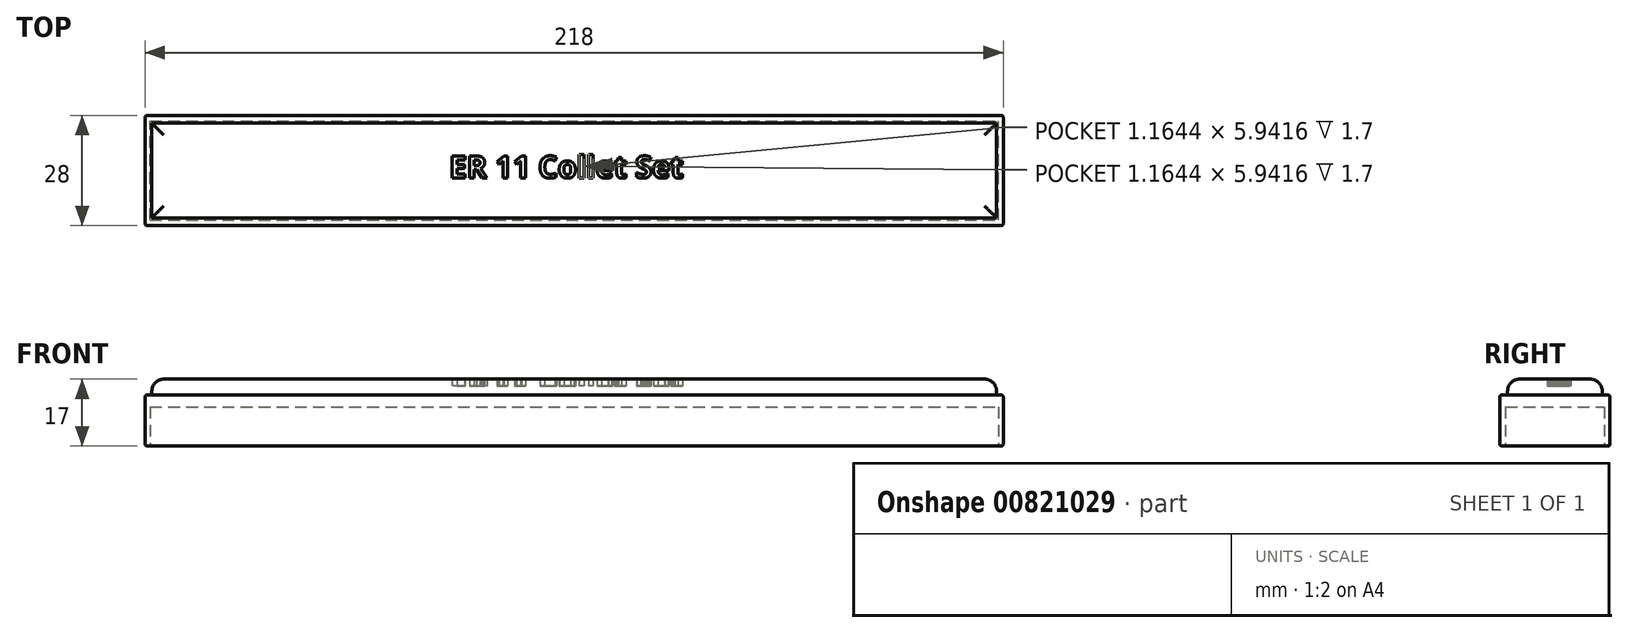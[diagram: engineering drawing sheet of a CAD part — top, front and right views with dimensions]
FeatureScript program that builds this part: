
annotation { "Feature Type Name" : "Feature", "Feature Type Description" : "" }
export const myFeature = defineFeature(function(context is Context, id is Id, definition is map)
    precondition{}
    {
        {
            var Q0;
            Q0=qCreatedBy(makeId("Top.planeOp"),FACE);
            var sketch = newSketch(context, id + "F0", { "sketchPlane" : qUnion([Q0])});
            skLineSegment(sketch, "E0.bottom", {"start": v(-109, 14) * mm, "end": v(109, 14) * mm});
            skLineSegment(sketch, "E0.top", {"start": v(-109, -14) * mm, "end": v(109, -14) * mm});
            skLineSegment(sketch, "E0.left", {"start": v(-109, 14) * mm, "end": v(-109, -14) * mm});
            skLineSegment(sketch, "E0.right", {"start": v(109, 14) * mm, "end": v(109, -14) * mm});
            skPoint(sketch, "E0.middle", {"position": v(0, 0) * mm});
            skLineSegment(sketch, "E1.bottom", {"start": v(-107.75, -12.6) * mm, "end": v(107.75, -12.6) * mm});
            skLineSegment(sketch, "E1.top", {"start": v(-107.75, 12.6) * mm, "end": v(107.75, 12.6) * mm});
            skLineSegment(sketch, "E1.left", {"start": v(-107.75, -12.6) * mm, "end": v(-107.75, 12.6) * mm});
            skLineSegment(sketch, "E1.right", {"start": v(107.75, -12.6) * mm, "end": v(107.75, 12.6) * mm});
            skSolve(sketch);
        }
        {
            var Q0;
            Q0=qSketchRegion(id+"F0",true);
            extrude(context, id + "F1", {"entities" : qUnion([Q0]), "depth" : 10 * mm, "offsetDistance" : 25 * mm});
        }
        {
            var Q0;
            Q0=makeQuery(id+"F1.opExtrude","CAP_FACE",FACE,{"disambiguationData":[OSD([sQuery(id+"F0.wireOp",EDGE,"E0.bottom"),sQuery(id+"F0.wireOp",EDGE,"E0.top"),sQuery(id+"F0.wireOp",EDGE,"E0.left"),sQuery(id+"F0.wireOp",EDGE,"E0.right"),sQuery(id+"F0.wireOp",EDGE,"E1.bottom"),sQuery(id+"F0.wireOp",EDGE,"E1.top"),sQuery(id+"F0.wireOp",EDGE,"E1.left"),sQuery(id+"F0.wireOp",EDGE,"E1.right")])],"isStart":false});
            var sketch = newSketch(context, id + "F2", { "sketchPlane" : qUnion([Q0])});
            skLineSegment(sketch, "E2.bottom", {"start": v(109, -14) * mm, "end": v(-109, -14) * mm});
            skLineSegment(sketch, "E2.top", {"start": v(109, 14) * mm, "end": v(-109, 14) * mm});
            skLineSegment(sketch, "E2.left", {"start": v(109, -14) * mm, "end": v(109, 14) * mm});
            skLineSegment(sketch, "E2.right", {"start": v(-109, -14) * mm, "end": v(-109, 14) * mm});
            skPoint(sketch, "E2.middle", {"position": v(0, 0) * mm});
            skText(sketch, "E3", { "text": "ER 11 Collet Set", "fontName": "OpenSans-Bold.ttf"});
            const initialGuessF2  = {"E3": [-0.03167, 0.03052, 1, 0, 0.00563]};
            skSetInitialGuess(sketch, initialGuessF2);
            skSolve(sketch);
        }
        {
            var Q0;
            Q0=qSketchRegion(id+"F2",true);
            extrude(context, id + "F3", {"entities" : qUnion([Q0]), "operationType" : NewBodyOperationType.ADD, "depth" : 3 * mm, "offsetDistance" : 25 * mm});
        }
        {
            var Q0;
            Q0=makeQuery(id+"F1.opExtrude","CAP_EDGE",EDGE,{"disambiguationData":[OSD([sQuery(id+"F0.wireOp",EDGE,"E0.top")])],"isStart":true});
            var Q1;
            Q1=makeQuery(id+"F1.opExtrude","CAP_EDGE",EDGE,{"disambiguationData":[OSD([sQuery(id+"F0.wireOp",EDGE,"E0.left")])],"isStart":true});
            var Q2;
            Q2=makeQuery(id+"F1.opExtrude","CAP_EDGE",EDGE,{"disambiguationData":[OSD([sQuery(id+"F0.wireOp",EDGE,"E0.right")])],"isStart":true});
            var Q3;
            Q3=makeQuery(id+"F3.boolean.opBoolean","MERGE",EDGE,{"derivedFrom":[makeQuery(id+"F1.opExtrude","SWEPT_EDGE",EDGE,{"disambiguationData":[OSD([sQuery(id+"F0.wireOp",EDGE,"E0.top"),sQuery(id+"F0.wireOp",EDGE,"E0.right")])]}),makeQuery(id+"F3.opExtrude","SWEPT_EDGE",EDGE,{"disambiguationData":[OSD([sQuery(id+"F2.wireOp",EDGE,"E2.bottom"),sQuery(id+"F2.wireOp",EDGE,"E2.left")])]})]});
            var Q4;
            Q4=makeQuery(id+"F3.opExtrude","CAP_EDGE",EDGE,{"disambiguationData":[OSD([sQuery(id+"F2.wireOp",EDGE,"E2.bottom")])],"isStart":false});
            var Q5;
            Q5=makeQuery(id+"F3.opExtrude","CAP_EDGE",EDGE,{"disambiguationData":[OSD([sQuery(id+"F2.wireOp",EDGE,"E2.left")])],"isStart":false});
            var Q6;
            Q6=makeQuery(id+"F3.opExtrude","CAP_EDGE",EDGE,{"disambiguationData":[OSD([sQuery(id+"F2.wireOp",EDGE,"E2.top")])],"isStart":false});
            var Q7;
            Q7=makeQuery(id+"F3.boolean.opBoolean","MERGE",FACE,{"derivedFrom":[makeQuery(id+"F1.opExtrude","SWEPT_FACE",FACE,{"disambiguationData":[OSD([sQuery(id+"F0.wireOp",EDGE,"E0.bottom")])]}),makeQuery(id+"F3.opExtrude","SWEPT_FACE",FACE,{"disambiguationData":[OSD([sQuery(id+"F2.wireOp",EDGE,"E2.top")])]})]});
            var Q8;
            Q8=makeQuery(id+"F1.opExtrude","CAP_EDGE",EDGE,{"disambiguationData":[OSD([sQuery(id+"F0.wireOp",EDGE,"E0.bottom")])],"isStart":true});
            var Q9;
            Q9=makeQuery(id+"F3.opExtrude","CAP_EDGE",EDGE,{"disambiguationData":[OSD([sQuery(id+"F2.wireOp",EDGE,"E2.right")])],"isStart":false});
            var Q10;
            Q10=makeQuery(id+"F3.boolean.opBoolean","MERGE",EDGE,{"derivedFrom":[makeQuery(id+"F1.opExtrude","SWEPT_EDGE",EDGE,{"disambiguationData":[OSD([sQuery(id+"F0.wireOp",EDGE,"E0.top"),sQuery(id+"F0.wireOp",EDGE,"E0.left")])]}),makeQuery(id+"F3.opExtrude","SWEPT_EDGE",EDGE,{"disambiguationData":[OSD([sQuery(id+"F2.wireOp",EDGE,"E2.bottom"),sQuery(id+"F2.wireOp",EDGE,"E2.right")])]})]});
            fillet(context, id + "F4", {"entities" : qUnion([Q0, Q1, Q2, Q3, Q4, Q5, Q6, Q7, Q8, Q9, Q10]), "radius" : .5 * mm, "tangentPropagation" : true, "allowEdgeOverflow" : false});
        }
        {
            var Q0;
            Q0=makeQuery(id+"F3.opExtrude","CAP_FACE",FACE,{"disambiguationData":[OSD([sQuery(id+"F2.wireOp",EDGE,"E2.bottom"),sQuery(id+"F2.wireOp",EDGE,"E2.top"),sQuery(id+"F2.wireOp",EDGE,"E2.left"),sQuery(id+"F2.wireOp",EDGE,"E2.right"),sQuery(id+"F2.wireOp",EDGE,"E3.sketch_text.stroke-0"),sQuery(id+"F2.wireOp",EDGE,"E3.sketch_text.stroke-1"),sQuery(id+"F2.wireOp",EDGE,"E3.sketch_text.stroke-2"),sQuery(id+"F2.wireOp",EDGE,"E3.sketch_text.stroke-3"),sQuery(id+"F2.wireOp",EDGE,"E3.sketch_text.stroke-4"),sQuery(id+"F2.wireOp",EDGE,"E3.sketch_text.stroke-5"),sQuery(id+"F2.wireOp",EDGE,"E3.sketch_text.stroke-6"),sQuery(id+"F2.wireOp",EDGE,"E3.sketch_text.stroke-7"),sQuery(id+"F2.wireOp",EDGE,"E3.sketch_text.stroke-8"),sQuery(id+"F2.wireOp",EDGE,"E3.sketch_text.stroke-9"),sQuery(id+"F2.wireOp",EDGE,"E3.sketch_text.stroke-10"),sQuery(id+"F2.wireOp",EDGE,"E3.sketch_text.stroke-11"),sQuery(id+"F2.wireOp",EDGE,"E3.sketch_text.stroke-19"),sQuery(id+"F2.wireOp",EDGE,"E3.sketch_text.stroke-20"),sQuery(id+"F2.wireOp",EDGE,"E3.sketch_text.stroke-21"),sQuery(id+"F2.wireOp",EDGE,"E3.sketch_text.stroke-22"),sQuery(id+"F2.wireOp",EDGE,"E3.sketch_text.stroke-23"),sQuery(id+"F2.wireOp",EDGE,"E3.sketch_text.stroke-24"),sQuery(id+"F2.wireOp",EDGE,"E3.sketch_text.stroke-25"),sQuery(id+"F2.wireOp",EDGE,"E3.sketch_text.stroke-26"),sQuery(id+"F2.wireOp",EDGE,"E3.sketch_text.stroke-27"),sQuery(id+"F2.wireOp",EDGE,"E3.sketch_text.stroke-28"),sQuery(id+"F2.wireOp",EDGE,"E3.sketch_text.stroke-29"),sQuery(id+"F2.wireOp",EDGE,"E3.sketch_text.stroke-30"),sQuery(id+"F2.wireOp",EDGE,"E3.sketch_text.stroke-31"),sQuery(id+"F2.wireOp",EDGE,"E3.sketch_text.stroke-32"),sQuery(id+"F2.wireOp",EDGE,"E3.sketch_text.stroke-33"),sQuery(id+"F2.wireOp",EDGE,"E3.sketch_text.stroke-34"),sQuery(id+"F2.wireOp",EDGE,"E3.sketch_text.stroke-35"),sQuery(id+"F2.wireOp",EDGE,"E3.sketch_text.stroke-36"),sQuery(id+"F2.wireOp",EDGE,"E3.sketch_text.stroke-37"),sQuery(id+"F2.wireOp",EDGE,"E3.sketch_text.stroke-38"),sQuery(id+"F2.wireOp",EDGE,"E3.sketch_text.stroke-39"),sQuery(id+"F2.wireOp",EDGE,"E3.sketch_text.stroke-40"),sQuery(id+"F2.wireOp",EDGE,"E3.sketch_text.stroke-41"),sQuery(id+"F2.wireOp",EDGE,"E3.sketch_text.stroke-42"),sQuery(id+"F2.wireOp",EDGE,"E3.sketch_text.stroke-43"),sQuery(id+"F2.wireOp",EDGE,"E3.sketch_text.stroke-44"),sQuery(id+"F2.wireOp",EDGE,"E3.sketch_text.stroke-45"),sQuery(id+"F2.wireOp",EDGE,"E3.sketch_text.stroke-46"),sQuery(id+"F2.wireOp",EDGE,"E3.sketch_text.stroke-47"),sQuery(id+"F2.wireOp",EDGE,"E3.sketch_text.stroke-48"),sQuery(id+"F2.wireOp",EDGE,"E3.sketch_text.stroke-49"),sQuery(id+"F2.wireOp",EDGE,"E3.sketch_text.stroke-50"),sQuery(id+"F2.wireOp",EDGE,"E3.sketch_text.stroke-51"),sQuery(id+"F2.wireOp",EDGE,"E3.sketch_text.stroke-52"),sQuery(id+"F2.wireOp",EDGE,"E3.sketch_text.stroke-53"),sQuery(id+"F2.wireOp",EDGE,"E3.sketch_text.stroke-54"),sQuery(id+"F2.wireOp",EDGE,"E3.sketch_text.stroke-55"),sQuery(id+"F2.wireOp",EDGE,"E3.sketch_text.stroke-56"),sQuery(id+"F2.wireOp",EDGE,"E3.sketch_text.stroke-57"),sQuery(id+"F2.wireOp",EDGE,"E3.sketch_text.stroke-58"),sQuery(id+"F2.wireOp",EDGE,"E3.sketch_text.stroke-59"),sQuery(id+"F2.wireOp",EDGE,"E3.sketch_text.stroke-60"),sQuery(id+"F2.wireOp",EDGE,"E3.sketch_text.stroke-61"),sQuery(id+"F2.wireOp",EDGE,"E3.sketch_text.stroke-62"),sQuery(id+"F2.wireOp",EDGE,"E3.sketch_text.stroke-63"),sQuery(id+"F2.wireOp",EDGE,"E3.sketch_text.stroke-64"),sQuery(id+"F2.wireOp",EDGE,"E3.sketch_text.stroke-65"),sQuery(id+"F2.wireOp",EDGE,"E3.sketch_text.stroke-74"),sQuery(id+"F2.wireOp",EDGE,"E3.sketch_text.stroke-75"),sQuery(id+"F2.wireOp",EDGE,"E3.sketch_text.stroke-76"),sQuery(id+"F2.wireOp",EDGE,"E3.sketch_text.stroke-77"),sQuery(id+"F2.wireOp",EDGE,"E3.sketch_text.stroke-78"),sQuery(id+"F2.wireOp",EDGE,"E3.sketch_text.stroke-79"),sQuery(id+"F2.wireOp",EDGE,"E3.sketch_text.stroke-80"),sQuery(id+"F2.wireOp",EDGE,"E3.sketch_text.stroke-81"),sQuery(id+"F2.wireOp",EDGE,"E3.sketch_text.stroke-82"),sQuery(id+"F2.wireOp",EDGE,"E3.sketch_text.stroke-83"),sQuery(id+"F2.wireOp",EDGE,"E3.sketch_text.stroke-84"),sQuery(id+"F2.wireOp",EDGE,"E3.sketch_text.stroke-85"),sQuery(id+"F2.wireOp",EDGE,"E3.sketch_text.stroke-86"),sQuery(id+"F2.wireOp",EDGE,"E3.sketch_text.stroke-87"),sQuery(id+"F2.wireOp",EDGE,"E3.sketch_text.stroke-88"),sQuery(id+"F2.wireOp",EDGE,"E3.sketch_text.stroke-89"),sQuery(id+"F2.wireOp",EDGE,"E3.sketch_text.stroke-90"),sQuery(id+"F2.wireOp",EDGE,"E3.sketch_text.stroke-91"),sQuery(id+"F2.wireOp",EDGE,"E3.sketch_text.stroke-97"),sQuery(id+"F2.wireOp",EDGE,"E3.sketch_text.stroke-98"),sQuery(id+"F2.wireOp",EDGE,"E3.sketch_text.stroke-99"),sQuery(id+"F2.wireOp",EDGE,"E3.sketch_text.stroke-100"),sQuery(id+"F2.wireOp",EDGE,"E3.sketch_text.stroke-101"),sQuery(id+"F2.wireOp",EDGE,"E3.sketch_text.stroke-102"),sQuery(id+"F2.wireOp",EDGE,"E3.sketch_text.stroke-103"),sQuery(id+"F2.wireOp",EDGE,"E3.sketch_text.stroke-104"),sQuery(id+"F2.wireOp",EDGE,"E3.sketch_text.stroke-105"),sQuery(id+"F2.wireOp",EDGE,"E3.sketch_text.stroke-106"),sQuery(id+"F2.wireOp",EDGE,"E3.sketch_text.stroke-107"),sQuery(id+"F2.wireOp",EDGE,"E3.sketch_text.stroke-108"),sQuery(id+"F2.wireOp",EDGE,"E3.sketch_text.stroke-109"),sQuery(id+"F2.wireOp",EDGE,"E3.sketch_text.stroke-110"),sQuery(id+"F2.wireOp",EDGE,"E3.sketch_text.stroke-111"),sQuery(id+"F2.wireOp",EDGE,"E3.sketch_text.stroke-112"),sQuery(id+"F2.wireOp",EDGE,"E3.sketch_text.stroke-113"),sQuery(id+"F2.wireOp",EDGE,"E3.sketch_text.stroke-114"),sQuery(id+"F2.wireOp",EDGE,"E3.sketch_text.stroke-115"),sQuery(id+"F2.wireOp",EDGE,"E3.sketch_text.stroke-116"),sQuery(id+"F2.wireOp",EDGE,"E3.sketch_text.stroke-117"),sQuery(id+"F2.wireOp",EDGE,"E3.sketch_text.stroke-118"),sQuery(id+"F2.wireOp",EDGE,"E3.sketch_text.stroke-119"),sQuery(id+"F2.wireOp",EDGE,"E3.sketch_text.stroke-120"),sQuery(id+"F2.wireOp",EDGE,"E3.sketch_text.stroke-121"),sQuery(id+"F2.wireOp",EDGE,"E3.sketch_text.stroke-122"),sQuery(id+"F2.wireOp",EDGE,"E3.sketch_text.stroke-123"),sQuery(id+"F2.wireOp",EDGE,"E3.sketch_text.stroke-124"),sQuery(id+"F2.wireOp",EDGE,"E3.sketch_text.stroke-125"),sQuery(id+"F2.wireOp",EDGE,"E3.sketch_text.stroke-126"),sQuery(id+"F2.wireOp",EDGE,"E3.sketch_text.stroke-127"),sQuery(id+"F2.wireOp",EDGE,"E3.sketch_text.stroke-128"),sQuery(id+"F2.wireOp",EDGE,"E3.sketch_text.stroke-129"),sQuery(id+"F2.wireOp",EDGE,"E3.sketch_text.stroke-130"),sQuery(id+"F2.wireOp",EDGE,"E3.sketch_text.stroke-131"),sQuery(id+"F2.wireOp",EDGE,"E3.sketch_text.stroke-132"),sQuery(id+"F2.wireOp",EDGE,"E3.sketch_text.stroke-133"),sQuery(id+"F2.wireOp",EDGE,"E3.sketch_text.stroke-134"),sQuery(id+"F2.wireOp",EDGE,"E3.sketch_text.stroke-135"),sQuery(id+"F2.wireOp",EDGE,"E3.sketch_text.stroke-136"),sQuery(id+"F2.wireOp",EDGE,"E3.sketch_text.stroke-137"),sQuery(id+"F2.wireOp",EDGE,"E3.sketch_text.stroke-138"),sQuery(id+"F2.wireOp",EDGE,"E3.sketch_text.stroke-139"),sQuery(id+"F2.wireOp",EDGE,"E3.sketch_text.stroke-140"),sQuery(id+"F2.wireOp",EDGE,"E3.sketch_text.stroke-141"),sQuery(id+"F2.wireOp",EDGE,"E3.sketch_text.stroke-142"),sQuery(id+"F2.wireOp",EDGE,"E3.sketch_text.stroke-143"),sQuery(id+"F2.wireOp",EDGE,"E3.sketch_text.stroke-144"),sQuery(id+"F2.wireOp",EDGE,"E3.sketch_text.stroke-145"),sQuery(id+"F2.wireOp",EDGE,"E3.sketch_text.stroke-146"),sQuery(id+"F2.wireOp",EDGE,"E3.sketch_text.stroke-147"),sQuery(id+"F2.wireOp",EDGE,"E3.sketch_text.stroke-148"),sQuery(id+"F2.wireOp",EDGE,"E3.sketch_text.stroke-149"),sQuery(id+"F2.wireOp",EDGE,"E3.sketch_text.stroke-150"),sQuery(id+"F2.wireOp",EDGE,"E3.sketch_text.stroke-151"),sQuery(id+"F2.wireOp",EDGE,"E3.sketch_text.stroke-152"),sQuery(id+"F2.wireOp",EDGE,"E3.sketch_text.stroke-153"),sQuery(id+"F2.wireOp",EDGE,"E3.sketch_text.stroke-154"),sQuery(id+"F2.wireOp",EDGE,"E3.sketch_text.stroke-155"),sQuery(id+"F2.wireOp",EDGE,"E3.sketch_text.stroke-156"),sQuery(id+"F2.wireOp",EDGE,"E3.sketch_text.stroke-157"),sQuery(id+"F2.wireOp",EDGE,"E3.sketch_text.stroke-163"),sQuery(id+"F2.wireOp",EDGE,"E3.sketch_text.stroke-164"),sQuery(id+"F2.wireOp",EDGE,"E3.sketch_text.stroke-165"),sQuery(id+"F2.wireOp",EDGE,"E3.sketch_text.stroke-166"),sQuery(id+"F2.wireOp",EDGE,"E3.sketch_text.stroke-167"),sQuery(id+"F2.wireOp",EDGE,"E3.sketch_text.stroke-168"),sQuery(id+"F2.wireOp",EDGE,"E3.sketch_text.stroke-169"),sQuery(id+"F2.wireOp",EDGE,"E3.sketch_text.stroke-170"),sQuery(id+"F2.wireOp",EDGE,"E3.sketch_text.stroke-171"),sQuery(id+"F2.wireOp",EDGE,"E3.sketch_text.stroke-172"),sQuery(id+"F2.wireOp",EDGE,"E3.sketch_text.stroke-173"),sQuery(id+"F2.wireOp",EDGE,"E3.sketch_text.stroke-174"),sQuery(id+"F2.wireOp",EDGE,"E3.sketch_text.stroke-175"),sQuery(id+"F2.wireOp",EDGE,"E3.sketch_text.stroke-176"),sQuery(id+"F2.wireOp",EDGE,"E3.sketch_text.stroke-177"),sQuery(id+"F2.wireOp",EDGE,"E3.sketch_text.stroke-178"),sQuery(id+"F2.wireOp",EDGE,"E3.sketch_text.stroke-179"),sQuery(id+"F2.wireOp",EDGE,"E3.sketch_text.stroke-180"),sQuery(id+"F2.wireOp",EDGE,"E3.sketch_text.stroke-181"),sQuery(id+"F2.wireOp",EDGE,"E3.sketch_text.stroke-182"),sQuery(id+"F2.wireOp",EDGE,"E3.sketch_text.stroke-183"),sQuery(id+"F2.wireOp",EDGE,"E3.sketch_text.stroke-184"),sQuery(id+"F2.wireOp",EDGE,"E3.sketch_text.stroke-185"),sQuery(id+"F2.wireOp",EDGE,"E3.sketch_text.stroke-186"),sQuery(id+"F2.wireOp",EDGE,"E3.sketch_text.stroke-187"),sQuery(id+"F2.wireOp",EDGE,"E3.sketch_text.stroke-188"),sQuery(id+"F2.wireOp",EDGE,"E3.sketch_text.stroke-189"),sQuery(id+"F2.wireOp",EDGE,"E3.sketch_text.stroke-190"),sQuery(id+"F2.wireOp",EDGE,"E3.sketch_text.stroke-191"),sQuery(id+"F2.wireOp",EDGE,"E3.sketch_text.stroke-192"),sQuery(id+"F2.wireOp",EDGE,"E3.sketch_text.stroke-193"),sQuery(id+"F2.wireOp",EDGE,"E3.sketch_text.stroke-194"),sQuery(id+"F2.wireOp",EDGE,"E3.sketch_text.stroke-195")])],"isStart":false});
            var sketch = newSketch(context, id + "F5", { "sketchPlane" : qUnion([Q0])});
            skLineSegment(sketch, "E4.bottom", {"start": v(-107.3, 12.02) * mm, "end": v(107.3, 12.02) * mm});
            skLineSegment(sketch, "E4.top", {"start": v(-107.3, -12.02) * mm, "end": v(107.3, -12.02) * mm});
            skLineSegment(sketch, "E4.left", {"start": v(-107.3, 12.02) * mm, "end": v(-107.3, -12.02) * mm});
            skLineSegment(sketch, "E4.right", {"start": v(107.3, 12.02) * mm, "end": v(107.3, -12.02) * mm});
            skPoint(sketch, "E4.middle", {"position": v(0, 0) * mm});
            skSolve(sketch);
        }
        {
            var Q0;
            Q0=qSketchRegion(id+"F5",true);
            extrude(context, id + "F6", {"entities" : qUnion([Q0]), "operationType" : NewBodyOperationType.ADD, "depth" : 4 * mm, "offsetDistance" : 25 * mm});
        }
        {
            var Q0;
            Q0=makeQuery(id+"F6.opExtrude","CAP_EDGE",EDGE,{"disambiguationData":[OSD([sQuery(id+"F5.wireOp",EDGE,"E4.top")])],"isStart":false});
            var Q1;
            Q1=makeQuery(id+"F6.opExtrude","CAP_EDGE",EDGE,{"disambiguationData":[OSD([sQuery(id+"F5.wireOp",EDGE,"E4.bottom")])],"isStart":false});
            var Q2;
            Q2=makeQuery(id+"F6.opExtrude","CAP_EDGE",EDGE,{"disambiguationData":[OSD([sQuery(id+"F5.wireOp",EDGE,"E4.left")])],"isStart":false});
            var Q3;
            Q3=makeQuery(id+"F6.opExtrude","CAP_EDGE",EDGE,{"disambiguationData":[OSD([sQuery(id+"F5.wireOp",EDGE,"E4.right")])],"isStart":false});
            fillet(context, id + "F7", {"entities" : qUnion([Q0, Q1, Q2, Q3]), "radius" : 3 * mm, "tangentPropagation" : true, "allowEdgeOverflow" : false});
        }
        {
            var Q0;
            Q0=makeQuery(id+"F3.opExtrude","SWEPT_BODY",BODY,{"disambiguationData":[OSD([sQuery(id+"F2.wireOp",EDGE,"E3.sketch_text.stroke-158"),sQuery(id+"F2.wireOp",EDGE,"E3.sketch_text.stroke-159"),sQuery(id+"F2.wireOp",EDGE,"E3.sketch_text.stroke-160"),sQuery(id+"F2.wireOp",EDGE,"E3.sketch_text.stroke-161"),sQuery(id+"F2.wireOp",EDGE,"E3.sketch_text.stroke-162"),sQuery(id+"F2.wireOp",EDGE,"E3.sketch_text.stroke-163"),sQuery(id+"F2.wireOp",EDGE,"E3.sketch_text.stroke-164"),sQuery(id+"F2.wireOp",EDGE,"E3.sketch_text.stroke-165"),sQuery(id+"F2.wireOp",EDGE,"E3.sketch_text.stroke-166"),sQuery(id+"F2.wireOp",EDGE,"E3.sketch_text.stroke-167"),sQuery(id+"F2.wireOp",EDGE,"E3.sketch_text.stroke-168"),sQuery(id+"F2.wireOp",EDGE,"E3.sketch_text.stroke-169"),sQuery(id+"F2.wireOp",EDGE,"E3.sketch_text.stroke-170"),sQuery(id+"F2.wireOp",EDGE,"E3.sketch_text.stroke-171"),sQuery(id+"F2.wireOp",EDGE,"E3.sketch_text.stroke-172"),sQuery(id+"F2.wireOp",EDGE,"E3.sketch_text.stroke-173"),sQuery(id+"F2.wireOp",EDGE,"E3.sketch_text.stroke-174"),sQuery(id+"F2.wireOp",EDGE,"E3.sketch_text.stroke-175"),sQuery(id+"F2.wireOp",EDGE,"E3.sketch_text.stroke-176"),sQuery(id+"F2.wireOp",EDGE,"E3.sketch_text.stroke-177")])]});
            var Q1;
            Q1=makeQuery(id+"F3.opExtrude","SWEPT_BODY",BODY,{"disambiguationData":[OSD([sQuery(id+"F2.wireOp",EDGE,"E3.sketch_text.stroke-0"),sQuery(id+"F2.wireOp",EDGE,"E3.sketch_text.stroke-1"),sQuery(id+"F2.wireOp",EDGE,"E3.sketch_text.stroke-2"),sQuery(id+"F2.wireOp",EDGE,"E3.sketch_text.stroke-3"),sQuery(id+"F2.wireOp",EDGE,"E3.sketch_text.stroke-4"),sQuery(id+"F2.wireOp",EDGE,"E3.sketch_text.stroke-5"),sQuery(id+"F2.wireOp",EDGE,"E3.sketch_text.stroke-6"),sQuery(id+"F2.wireOp",EDGE,"E3.sketch_text.stroke-7"),sQuery(id+"F2.wireOp",EDGE,"E3.sketch_text.stroke-8"),sQuery(id+"F2.wireOp",EDGE,"E3.sketch_text.stroke-9"),sQuery(id+"F2.wireOp",EDGE,"E3.sketch_text.stroke-10"),sQuery(id+"F2.wireOp",EDGE,"E3.sketch_text.stroke-11")])]});
            var Q2;
            Q2=makeQuery(id+"F3.opExtrude","SWEPT_BODY",BODY,{"disambiguationData":[OSD([sQuery(id+"F2.wireOp",EDGE,"E3.sketch_text.stroke-12"),sQuery(id+"F2.wireOp",EDGE,"E3.sketch_text.stroke-13"),sQuery(id+"F2.wireOp",EDGE,"E3.sketch_text.stroke-14"),sQuery(id+"F2.wireOp",EDGE,"E3.sketch_text.stroke-15"),sQuery(id+"F2.wireOp",EDGE,"E3.sketch_text.stroke-16"),sQuery(id+"F2.wireOp",EDGE,"E3.sketch_text.stroke-17"),sQuery(id+"F2.wireOp",EDGE,"E3.sketch_text.stroke-18"),sQuery(id+"F2.wireOp",EDGE,"E3.sketch_text.stroke-19"),sQuery(id+"F2.wireOp",EDGE,"E3.sketch_text.stroke-20"),sQuery(id+"F2.wireOp",EDGE,"E3.sketch_text.stroke-21"),sQuery(id+"F2.wireOp",EDGE,"E3.sketch_text.stroke-22"),sQuery(id+"F2.wireOp",EDGE,"E3.sketch_text.stroke-23"),sQuery(id+"F2.wireOp",EDGE,"E3.sketch_text.stroke-24"),sQuery(id+"F2.wireOp",EDGE,"E3.sketch_text.stroke-25"),sQuery(id+"F2.wireOp",EDGE,"E3.sketch_text.stroke-26"),sQuery(id+"F2.wireOp",EDGE,"E3.sketch_text.stroke-27"),sQuery(id+"F2.wireOp",EDGE,"E3.sketch_text.stroke-28"),sQuery(id+"F2.wireOp",EDGE,"E3.sketch_text.stroke-29"),sQuery(id+"F2.wireOp",EDGE,"E3.sketch_text.stroke-30")])]});
            var Q3;
            Q3=makeQuery(id+"F3.opExtrude","SWEPT_BODY",BODY,{"disambiguationData":[OSD([sQuery(id+"F2.wireOp",EDGE,"E3.sketch_text.stroke-41"),sQuery(id+"F2.wireOp",EDGE,"E3.sketch_text.stroke-42"),sQuery(id+"F2.wireOp",EDGE,"E3.sketch_text.stroke-43"),sQuery(id+"F2.wireOp",EDGE,"E3.sketch_text.stroke-44"),sQuery(id+"F2.wireOp",EDGE,"E3.sketch_text.stroke-45"),sQuery(id+"F2.wireOp",EDGE,"E3.sketch_text.stroke-46"),sQuery(id+"F2.wireOp",EDGE,"E3.sketch_text.stroke-47"),sQuery(id+"F2.wireOp",EDGE,"E3.sketch_text.stroke-48"),sQuery(id+"F2.wireOp",EDGE,"E3.sketch_text.stroke-49"),sQuery(id+"F2.wireOp",EDGE,"E3.sketch_text.stroke-50")])]});
            var Q4;
            Q4=makeQuery(id+"F3.opExtrude","SWEPT_BODY",BODY,{"disambiguationData":[OSD([sQuery(id+"F2.wireOp",EDGE,"E3.sketch_text.stroke-31"),sQuery(id+"F2.wireOp",EDGE,"E3.sketch_text.stroke-32"),sQuery(id+"F2.wireOp",EDGE,"E3.sketch_text.stroke-33"),sQuery(id+"F2.wireOp",EDGE,"E3.sketch_text.stroke-34"),sQuery(id+"F2.wireOp",EDGE,"E3.sketch_text.stroke-35"),sQuery(id+"F2.wireOp",EDGE,"E3.sketch_text.stroke-36"),sQuery(id+"F2.wireOp",EDGE,"E3.sketch_text.stroke-37"),sQuery(id+"F2.wireOp",EDGE,"E3.sketch_text.stroke-38"),sQuery(id+"F2.wireOp",EDGE,"E3.sketch_text.stroke-39"),sQuery(id+"F2.wireOp",EDGE,"E3.sketch_text.stroke-40")])]});
            var Q5;
            Q5=makeQuery(id+"F3.opExtrude","SWEPT_BODY",BODY,{"disambiguationData":[OSD([sQuery(id+"F2.wireOp",EDGE,"E3.sketch_text.stroke-66"),sQuery(id+"F2.wireOp",EDGE,"E3.sketch_text.stroke-67"),sQuery(id+"F2.wireOp",EDGE,"E3.sketch_text.stroke-68"),sQuery(id+"F2.wireOp",EDGE,"E3.sketch_text.stroke-69"),sQuery(id+"F2.wireOp",EDGE,"E3.sketch_text.stroke-70"),sQuery(id+"F2.wireOp",EDGE,"E3.sketch_text.stroke-71"),sQuery(id+"F2.wireOp",EDGE,"E3.sketch_text.stroke-72"),sQuery(id+"F2.wireOp",EDGE,"E3.sketch_text.stroke-73"),sQuery(id+"F2.wireOp",EDGE,"E3.sketch_text.stroke-74"),sQuery(id+"F2.wireOp",EDGE,"E3.sketch_text.stroke-75"),sQuery(id+"F2.wireOp",EDGE,"E3.sketch_text.stroke-76"),sQuery(id+"F2.wireOp",EDGE,"E3.sketch_text.stroke-77"),sQuery(id+"F2.wireOp",EDGE,"E3.sketch_text.stroke-78"),sQuery(id+"F2.wireOp",EDGE,"E3.sketch_text.stroke-79"),sQuery(id+"F2.wireOp",EDGE,"E3.sketch_text.stroke-80"),sQuery(id+"F2.wireOp",EDGE,"E3.sketch_text.stroke-81"),sQuery(id+"F2.wireOp",EDGE,"E3.sketch_text.stroke-82"),sQuery(id+"F2.wireOp",EDGE,"E3.sketch_text.stroke-83")])]});
            var Q6;
            Q6=makeQuery(id+"F3.opExtrude","SWEPT_BODY",BODY,{"disambiguationData":[OSD([sQuery(id+"F2.wireOp",EDGE,"E3.sketch_text.stroke-51"),sQuery(id+"F2.wireOp",EDGE,"E3.sketch_text.stroke-52"),sQuery(id+"F2.wireOp",EDGE,"E3.sketch_text.stroke-53"),sQuery(id+"F2.wireOp",EDGE,"E3.sketch_text.stroke-54"),sQuery(id+"F2.wireOp",EDGE,"E3.sketch_text.stroke-55"),sQuery(id+"F2.wireOp",EDGE,"E3.sketch_text.stroke-56"),sQuery(id+"F2.wireOp",EDGE,"E3.sketch_text.stroke-57"),sQuery(id+"F2.wireOp",EDGE,"E3.sketch_text.stroke-58"),sQuery(id+"F2.wireOp",EDGE,"E3.sketch_text.stroke-59"),sQuery(id+"F2.wireOp",EDGE,"E3.sketch_text.stroke-60"),sQuery(id+"F2.wireOp",EDGE,"E3.sketch_text.stroke-61"),sQuery(id+"F2.wireOp",EDGE,"E3.sketch_text.stroke-62"),sQuery(id+"F2.wireOp",EDGE,"E3.sketch_text.stroke-63"),sQuery(id+"F2.wireOp",EDGE,"E3.sketch_text.stroke-64"),sQuery(id+"F2.wireOp",EDGE,"E3.sketch_text.stroke-65")])]});
            var Q7;
            Q7=makeQuery(id+"F3.opExtrude","SWEPT_BODY",BODY,{"disambiguationData":[OSD([sQuery(id+"F2.wireOp",EDGE,"E3.sketch_text.stroke-84"),sQuery(id+"F2.wireOp",EDGE,"E3.sketch_text.stroke-85"),sQuery(id+"F2.wireOp",EDGE,"E3.sketch_text.stroke-86"),sQuery(id+"F2.wireOp",EDGE,"E3.sketch_text.stroke-87")])]});
            var Q8;
            Q8=makeQuery(id+"F3.opExtrude","SWEPT_BODY",BODY,{"disambiguationData":[OSD([sQuery(id+"F2.wireOp",EDGE,"E3.sketch_text.stroke-88"),sQuery(id+"F2.wireOp",EDGE,"E3.sketch_text.stroke-89"),sQuery(id+"F2.wireOp",EDGE,"E3.sketch_text.stroke-90"),sQuery(id+"F2.wireOp",EDGE,"E3.sketch_text.stroke-91")])]});
            var Q9;
            Q9=makeQuery(id+"F3.opExtrude","SWEPT_BODY",BODY,{"disambiguationData":[OSD([sQuery(id+"F2.wireOp",EDGE,"E3.sketch_text.stroke-92"),sQuery(id+"F2.wireOp",EDGE,"E3.sketch_text.stroke-93"),sQuery(id+"F2.wireOp",EDGE,"E3.sketch_text.stroke-94"),sQuery(id+"F2.wireOp",EDGE,"E3.sketch_text.stroke-95"),sQuery(id+"F2.wireOp",EDGE,"E3.sketch_text.stroke-96"),sQuery(id+"F2.wireOp",EDGE,"E3.sketch_text.stroke-97"),sQuery(id+"F2.wireOp",EDGE,"E3.sketch_text.stroke-98"),sQuery(id+"F2.wireOp",EDGE,"E3.sketch_text.stroke-99"),sQuery(id+"F2.wireOp",EDGE,"E3.sketch_text.stroke-100"),sQuery(id+"F2.wireOp",EDGE,"E3.sketch_text.stroke-101"),sQuery(id+"F2.wireOp",EDGE,"E3.sketch_text.stroke-102"),sQuery(id+"F2.wireOp",EDGE,"E3.sketch_text.stroke-103"),sQuery(id+"F2.wireOp",EDGE,"E3.sketch_text.stroke-104"),sQuery(id+"F2.wireOp",EDGE,"E3.sketch_text.stroke-105"),sQuery(id+"F2.wireOp",EDGE,"E3.sketch_text.stroke-106"),sQuery(id+"F2.wireOp",EDGE,"E3.sketch_text.stroke-107"),sQuery(id+"F2.wireOp",EDGE,"E3.sketch_text.stroke-108"),sQuery(id+"F2.wireOp",EDGE,"E3.sketch_text.stroke-109"),sQuery(id+"F2.wireOp",EDGE,"E3.sketch_text.stroke-110"),sQuery(id+"F2.wireOp",EDGE,"E3.sketch_text.stroke-111")])]});
            var Q10;
            Q10=makeQuery(id+"F3.opExtrude","SWEPT_BODY",BODY,{"disambiguationData":[OSD([sQuery(id+"F2.wireOp",EDGE,"E3.sketch_text.stroke-112"),sQuery(id+"F2.wireOp",EDGE,"E3.sketch_text.stroke-113"),sQuery(id+"F2.wireOp",EDGE,"E3.sketch_text.stroke-114"),sQuery(id+"F2.wireOp",EDGE,"E3.sketch_text.stroke-115"),sQuery(id+"F2.wireOp",EDGE,"E3.sketch_text.stroke-116"),sQuery(id+"F2.wireOp",EDGE,"E3.sketch_text.stroke-117"),sQuery(id+"F2.wireOp",EDGE,"E3.sketch_text.stroke-118"),sQuery(id+"F2.wireOp",EDGE,"E3.sketch_text.stroke-119"),sQuery(id+"F2.wireOp",EDGE,"E3.sketch_text.stroke-120"),sQuery(id+"F2.wireOp",EDGE,"E3.sketch_text.stroke-121"),sQuery(id+"F2.wireOp",EDGE,"E3.sketch_text.stroke-122"),sQuery(id+"F2.wireOp",EDGE,"E3.sketch_text.stroke-123"),sQuery(id+"F2.wireOp",EDGE,"E3.sketch_text.stroke-124"),sQuery(id+"F2.wireOp",EDGE,"E3.sketch_text.stroke-125"),sQuery(id+"F2.wireOp",EDGE,"E3.sketch_text.stroke-126"),sQuery(id+"F2.wireOp",EDGE,"E3.sketch_text.stroke-127"),sQuery(id+"F2.wireOp",EDGE,"E3.sketch_text.stroke-128"),sQuery(id+"F2.wireOp",EDGE,"E3.sketch_text.stroke-129")])]});
            var Q11;
            Q11=makeQuery(id+"F3.opExtrude","SWEPT_BODY",BODY,{"disambiguationData":[OSD([sQuery(id+"F2.wireOp",EDGE,"E3.sketch_text.stroke-130"),sQuery(id+"F2.wireOp",EDGE,"E3.sketch_text.stroke-131"),sQuery(id+"F2.wireOp",EDGE,"E3.sketch_text.stroke-132"),sQuery(id+"F2.wireOp",EDGE,"E3.sketch_text.stroke-133"),sQuery(id+"F2.wireOp",EDGE,"E3.sketch_text.stroke-134"),sQuery(id+"F2.wireOp",EDGE,"E3.sketch_text.stroke-135"),sQuery(id+"F2.wireOp",EDGE,"E3.sketch_text.stroke-136"),sQuery(id+"F2.wireOp",EDGE,"E3.sketch_text.stroke-137"),sQuery(id+"F2.wireOp",EDGE,"E3.sketch_text.stroke-138"),sQuery(id+"F2.wireOp",EDGE,"E3.sketch_text.stroke-139"),sQuery(id+"F2.wireOp",EDGE,"E3.sketch_text.stroke-140"),sQuery(id+"F2.wireOp",EDGE,"E3.sketch_text.stroke-141"),sQuery(id+"F2.wireOp",EDGE,"E3.sketch_text.stroke-142"),sQuery(id+"F2.wireOp",EDGE,"E3.sketch_text.stroke-143"),sQuery(id+"F2.wireOp",EDGE,"E3.sketch_text.stroke-144"),sQuery(id+"F2.wireOp",EDGE,"E3.sketch_text.stroke-145"),sQuery(id+"F2.wireOp",EDGE,"E3.sketch_text.stroke-146"),sQuery(id+"F2.wireOp",EDGE,"E3.sketch_text.stroke-147"),sQuery(id+"F2.wireOp",EDGE,"E3.sketch_text.stroke-148"),sQuery(id+"F2.wireOp",EDGE,"E3.sketch_text.stroke-149"),sQuery(id+"F2.wireOp",EDGE,"E3.sketch_text.stroke-150"),sQuery(id+"F2.wireOp",EDGE,"E3.sketch_text.stroke-151"),sQuery(id+"F2.wireOp",EDGE,"E3.sketch_text.stroke-152"),sQuery(id+"F2.wireOp",EDGE,"E3.sketch_text.stroke-153"),sQuery(id+"F2.wireOp",EDGE,"E3.sketch_text.stroke-154"),sQuery(id+"F2.wireOp",EDGE,"E3.sketch_text.stroke-155"),sQuery(id+"F2.wireOp",EDGE,"E3.sketch_text.stroke-156"),sQuery(id+"F2.wireOp",EDGE,"E3.sketch_text.stroke-157")])]});
            var Q12;
            Q12=makeQuery(id+"F3.opExtrude","SWEPT_BODY",BODY,{"disambiguationData":[OSD([sQuery(id+"F2.wireOp",EDGE,"E3.sketch_text.stroke-178"),sQuery(id+"F2.wireOp",EDGE,"E3.sketch_text.stroke-179"),sQuery(id+"F2.wireOp",EDGE,"E3.sketch_text.stroke-180"),sQuery(id+"F2.wireOp",EDGE,"E3.sketch_text.stroke-181"),sQuery(id+"F2.wireOp",EDGE,"E3.sketch_text.stroke-182"),sQuery(id+"F2.wireOp",EDGE,"E3.sketch_text.stroke-183"),sQuery(id+"F2.wireOp",EDGE,"E3.sketch_text.stroke-184"),sQuery(id+"F2.wireOp",EDGE,"E3.sketch_text.stroke-185"),sQuery(id+"F2.wireOp",EDGE,"E3.sketch_text.stroke-186"),sQuery(id+"F2.wireOp",EDGE,"E3.sketch_text.stroke-187"),sQuery(id+"F2.wireOp",EDGE,"E3.sketch_text.stroke-188"),sQuery(id+"F2.wireOp",EDGE,"E3.sketch_text.stroke-189"),sQuery(id+"F2.wireOp",EDGE,"E3.sketch_text.stroke-190"),sQuery(id+"F2.wireOp",EDGE,"E3.sketch_text.stroke-191"),sQuery(id+"F2.wireOp",EDGE,"E3.sketch_text.stroke-192"),sQuery(id+"F2.wireOp",EDGE,"E3.sketch_text.stroke-193"),sQuery(id+"F2.wireOp",EDGE,"E3.sketch_text.stroke-194"),sQuery(id+"F2.wireOp",EDGE,"E3.sketch_text.stroke-195")])]});
            transform(context, id + "F8", {"entities" : qUnion([Q0, Q1, Q2, Q3, Q4, Q5, Q6, Q7, Q8, Q9, Q10, Q11, Q12]), "transformType" : TransformType.TRANSLATION_3D, "dx" : 0 * mm, "dy" : -32.4 * mm, "dz" : 6.6 * mm, "makeCopy" : false});
        }
        {
            var Q0;
            Q0=makeQuery(id+"F3.opExtrude","SWEPT_BODY",BODY,{"disambiguationData":[OSD([sQuery(id+"F2.wireOp",EDGE,"E3.sketch_text.stroke-0"),sQuery(id+"F2.wireOp",EDGE,"E3.sketch_text.stroke-1"),sQuery(id+"F2.wireOp",EDGE,"E3.sketch_text.stroke-2"),sQuery(id+"F2.wireOp",EDGE,"E3.sketch_text.stroke-3"),sQuery(id+"F2.wireOp",EDGE,"E3.sketch_text.stroke-4"),sQuery(id+"F2.wireOp",EDGE,"E3.sketch_text.stroke-5"),sQuery(id+"F2.wireOp",EDGE,"E3.sketch_text.stroke-6"),sQuery(id+"F2.wireOp",EDGE,"E3.sketch_text.stroke-7"),sQuery(id+"F2.wireOp",EDGE,"E3.sketch_text.stroke-8"),sQuery(id+"F2.wireOp",EDGE,"E3.sketch_text.stroke-9"),sQuery(id+"F2.wireOp",EDGE,"E3.sketch_text.stroke-10"),sQuery(id+"F2.wireOp",EDGE,"E3.sketch_text.stroke-11")])]});
            var Q1;
            Q1=makeQuery(id+"F3.opExtrude","SWEPT_BODY",BODY,{"disambiguationData":[OSD([sQuery(id+"F2.wireOp",EDGE,"E3.sketch_text.stroke-12"),sQuery(id+"F2.wireOp",EDGE,"E3.sketch_text.stroke-13"),sQuery(id+"F2.wireOp",EDGE,"E3.sketch_text.stroke-14"),sQuery(id+"F2.wireOp",EDGE,"E3.sketch_text.stroke-15"),sQuery(id+"F2.wireOp",EDGE,"E3.sketch_text.stroke-16"),sQuery(id+"F2.wireOp",EDGE,"E3.sketch_text.stroke-17"),sQuery(id+"F2.wireOp",EDGE,"E3.sketch_text.stroke-18"),sQuery(id+"F2.wireOp",EDGE,"E3.sketch_text.stroke-19"),sQuery(id+"F2.wireOp",EDGE,"E3.sketch_text.stroke-20"),sQuery(id+"F2.wireOp",EDGE,"E3.sketch_text.stroke-21"),sQuery(id+"F2.wireOp",EDGE,"E3.sketch_text.stroke-22"),sQuery(id+"F2.wireOp",EDGE,"E3.sketch_text.stroke-23"),sQuery(id+"F2.wireOp",EDGE,"E3.sketch_text.stroke-24"),sQuery(id+"F2.wireOp",EDGE,"E3.sketch_text.stroke-25"),sQuery(id+"F2.wireOp",EDGE,"E3.sketch_text.stroke-26"),sQuery(id+"F2.wireOp",EDGE,"E3.sketch_text.stroke-27"),sQuery(id+"F2.wireOp",EDGE,"E3.sketch_text.stroke-28"),sQuery(id+"F2.wireOp",EDGE,"E3.sketch_text.stroke-29"),sQuery(id+"F2.wireOp",EDGE,"E3.sketch_text.stroke-30")])]});
            var Q2;
            Q2=makeQuery(id+"F3.opExtrude","SWEPT_BODY",BODY,{"disambiguationData":[OSD([sQuery(id+"F2.wireOp",EDGE,"E3.sketch_text.stroke-41"),sQuery(id+"F2.wireOp",EDGE,"E3.sketch_text.stroke-42"),sQuery(id+"F2.wireOp",EDGE,"E3.sketch_text.stroke-43"),sQuery(id+"F2.wireOp",EDGE,"E3.sketch_text.stroke-44"),sQuery(id+"F2.wireOp",EDGE,"E3.sketch_text.stroke-45"),sQuery(id+"F2.wireOp",EDGE,"E3.sketch_text.stroke-46"),sQuery(id+"F2.wireOp",EDGE,"E3.sketch_text.stroke-47"),sQuery(id+"F2.wireOp",EDGE,"E3.sketch_text.stroke-48"),sQuery(id+"F2.wireOp",EDGE,"E3.sketch_text.stroke-49"),sQuery(id+"F2.wireOp",EDGE,"E3.sketch_text.stroke-50")])]});
            var Q3;
            Q3=makeQuery(id+"F3.opExtrude","SWEPT_BODY",BODY,{"disambiguationData":[OSD([sQuery(id+"F2.wireOp",EDGE,"E3.sketch_text.stroke-31"),sQuery(id+"F2.wireOp",EDGE,"E3.sketch_text.stroke-32"),sQuery(id+"F2.wireOp",EDGE,"E3.sketch_text.stroke-33"),sQuery(id+"F2.wireOp",EDGE,"E3.sketch_text.stroke-34"),sQuery(id+"F2.wireOp",EDGE,"E3.sketch_text.stroke-35"),sQuery(id+"F2.wireOp",EDGE,"E3.sketch_text.stroke-36"),sQuery(id+"F2.wireOp",EDGE,"E3.sketch_text.stroke-37"),sQuery(id+"F2.wireOp",EDGE,"E3.sketch_text.stroke-38"),sQuery(id+"F2.wireOp",EDGE,"E3.sketch_text.stroke-39"),sQuery(id+"F2.wireOp",EDGE,"E3.sketch_text.stroke-40")])]});
            var Q4;
            Q4=makeQuery(id+"F3.opExtrude","SWEPT_BODY",BODY,{"disambiguationData":[OSD([sQuery(id+"F2.wireOp",EDGE,"E3.sketch_text.stroke-66"),sQuery(id+"F2.wireOp",EDGE,"E3.sketch_text.stroke-67"),sQuery(id+"F2.wireOp",EDGE,"E3.sketch_text.stroke-68"),sQuery(id+"F2.wireOp",EDGE,"E3.sketch_text.stroke-69"),sQuery(id+"F2.wireOp",EDGE,"E3.sketch_text.stroke-70"),sQuery(id+"F2.wireOp",EDGE,"E3.sketch_text.stroke-71"),sQuery(id+"F2.wireOp",EDGE,"E3.sketch_text.stroke-72"),sQuery(id+"F2.wireOp",EDGE,"E3.sketch_text.stroke-73"),sQuery(id+"F2.wireOp",EDGE,"E3.sketch_text.stroke-74"),sQuery(id+"F2.wireOp",EDGE,"E3.sketch_text.stroke-75"),sQuery(id+"F2.wireOp",EDGE,"E3.sketch_text.stroke-76"),sQuery(id+"F2.wireOp",EDGE,"E3.sketch_text.stroke-77"),sQuery(id+"F2.wireOp",EDGE,"E3.sketch_text.stroke-78"),sQuery(id+"F2.wireOp",EDGE,"E3.sketch_text.stroke-79"),sQuery(id+"F2.wireOp",EDGE,"E3.sketch_text.stroke-80"),sQuery(id+"F2.wireOp",EDGE,"E3.sketch_text.stroke-81"),sQuery(id+"F2.wireOp",EDGE,"E3.sketch_text.stroke-82"),sQuery(id+"F2.wireOp",EDGE,"E3.sketch_text.stroke-83")])]});
            var Q5;
            Q5=makeQuery(id+"F3.opExtrude","SWEPT_BODY",BODY,{"disambiguationData":[OSD([sQuery(id+"F2.wireOp",EDGE,"E3.sketch_text.stroke-51"),sQuery(id+"F2.wireOp",EDGE,"E3.sketch_text.stroke-52"),sQuery(id+"F2.wireOp",EDGE,"E3.sketch_text.stroke-53"),sQuery(id+"F2.wireOp",EDGE,"E3.sketch_text.stroke-54"),sQuery(id+"F2.wireOp",EDGE,"E3.sketch_text.stroke-55"),sQuery(id+"F2.wireOp",EDGE,"E3.sketch_text.stroke-56"),sQuery(id+"F2.wireOp",EDGE,"E3.sketch_text.stroke-57"),sQuery(id+"F2.wireOp",EDGE,"E3.sketch_text.stroke-58"),sQuery(id+"F2.wireOp",EDGE,"E3.sketch_text.stroke-59"),sQuery(id+"F2.wireOp",EDGE,"E3.sketch_text.stroke-60"),sQuery(id+"F2.wireOp",EDGE,"E3.sketch_text.stroke-61"),sQuery(id+"F2.wireOp",EDGE,"E3.sketch_text.stroke-62"),sQuery(id+"F2.wireOp",EDGE,"E3.sketch_text.stroke-63"),sQuery(id+"F2.wireOp",EDGE,"E3.sketch_text.stroke-64"),sQuery(id+"F2.wireOp",EDGE,"E3.sketch_text.stroke-65")])]});
            var Q6;
            Q6=makeQuery(id+"F3.opExtrude","SWEPT_BODY",BODY,{"disambiguationData":[OSD([sQuery(id+"F2.wireOp",EDGE,"E3.sketch_text.stroke-84"),sQuery(id+"F2.wireOp",EDGE,"E3.sketch_text.stroke-85"),sQuery(id+"F2.wireOp",EDGE,"E3.sketch_text.stroke-86"),sQuery(id+"F2.wireOp",EDGE,"E3.sketch_text.stroke-87")])]});
            var Q7;
            Q7=makeQuery(id+"F3.opExtrude","SWEPT_BODY",BODY,{"disambiguationData":[OSD([sQuery(id+"F2.wireOp",EDGE,"E3.sketch_text.stroke-88"),sQuery(id+"F2.wireOp",EDGE,"E3.sketch_text.stroke-89"),sQuery(id+"F2.wireOp",EDGE,"E3.sketch_text.stroke-90"),sQuery(id+"F2.wireOp",EDGE,"E3.sketch_text.stroke-91")])]});
            var Q8;
            Q8=makeQuery(id+"F3.opExtrude","SWEPT_BODY",BODY,{"disambiguationData":[OSD([sQuery(id+"F2.wireOp",EDGE,"E3.sketch_text.stroke-92"),sQuery(id+"F2.wireOp",EDGE,"E3.sketch_text.stroke-93"),sQuery(id+"F2.wireOp",EDGE,"E3.sketch_text.stroke-94"),sQuery(id+"F2.wireOp",EDGE,"E3.sketch_text.stroke-95"),sQuery(id+"F2.wireOp",EDGE,"E3.sketch_text.stroke-96"),sQuery(id+"F2.wireOp",EDGE,"E3.sketch_text.stroke-97"),sQuery(id+"F2.wireOp",EDGE,"E3.sketch_text.stroke-98"),sQuery(id+"F2.wireOp",EDGE,"E3.sketch_text.stroke-99"),sQuery(id+"F2.wireOp",EDGE,"E3.sketch_text.stroke-100"),sQuery(id+"F2.wireOp",EDGE,"E3.sketch_text.stroke-101"),sQuery(id+"F2.wireOp",EDGE,"E3.sketch_text.stroke-102"),sQuery(id+"F2.wireOp",EDGE,"E3.sketch_text.stroke-103"),sQuery(id+"F2.wireOp",EDGE,"E3.sketch_text.stroke-104"),sQuery(id+"F2.wireOp",EDGE,"E3.sketch_text.stroke-105"),sQuery(id+"F2.wireOp",EDGE,"E3.sketch_text.stroke-106"),sQuery(id+"F2.wireOp",EDGE,"E3.sketch_text.stroke-107"),sQuery(id+"F2.wireOp",EDGE,"E3.sketch_text.stroke-108"),sQuery(id+"F2.wireOp",EDGE,"E3.sketch_text.stroke-109"),sQuery(id+"F2.wireOp",EDGE,"E3.sketch_text.stroke-110"),sQuery(id+"F2.wireOp",EDGE,"E3.sketch_text.stroke-111")])]});
            var Q9;
            Q9=makeQuery(id+"F3.opExtrude","SWEPT_BODY",BODY,{"disambiguationData":[OSD([sQuery(id+"F2.wireOp",EDGE,"E3.sketch_text.stroke-112"),sQuery(id+"F2.wireOp",EDGE,"E3.sketch_text.stroke-113"),sQuery(id+"F2.wireOp",EDGE,"E3.sketch_text.stroke-114"),sQuery(id+"F2.wireOp",EDGE,"E3.sketch_text.stroke-115"),sQuery(id+"F2.wireOp",EDGE,"E3.sketch_text.stroke-116"),sQuery(id+"F2.wireOp",EDGE,"E3.sketch_text.stroke-117"),sQuery(id+"F2.wireOp",EDGE,"E3.sketch_text.stroke-118"),sQuery(id+"F2.wireOp",EDGE,"E3.sketch_text.stroke-119"),sQuery(id+"F2.wireOp",EDGE,"E3.sketch_text.stroke-120"),sQuery(id+"F2.wireOp",EDGE,"E3.sketch_text.stroke-121"),sQuery(id+"F2.wireOp",EDGE,"E3.sketch_text.stroke-122"),sQuery(id+"F2.wireOp",EDGE,"E3.sketch_text.stroke-123"),sQuery(id+"F2.wireOp",EDGE,"E3.sketch_text.stroke-124"),sQuery(id+"F2.wireOp",EDGE,"E3.sketch_text.stroke-125"),sQuery(id+"F2.wireOp",EDGE,"E3.sketch_text.stroke-126"),sQuery(id+"F2.wireOp",EDGE,"E3.sketch_text.stroke-127"),sQuery(id+"F2.wireOp",EDGE,"E3.sketch_text.stroke-128"),sQuery(id+"F2.wireOp",EDGE,"E3.sketch_text.stroke-129")])]});
            var Q10;
            Q10=makeQuery(id+"F3.opExtrude","SWEPT_BODY",BODY,{"disambiguationData":[OSD([sQuery(id+"F2.wireOp",EDGE,"E3.sketch_text.stroke-130"),sQuery(id+"F2.wireOp",EDGE,"E3.sketch_text.stroke-131"),sQuery(id+"F2.wireOp",EDGE,"E3.sketch_text.stroke-132"),sQuery(id+"F2.wireOp",EDGE,"E3.sketch_text.stroke-133"),sQuery(id+"F2.wireOp",EDGE,"E3.sketch_text.stroke-134"),sQuery(id+"F2.wireOp",EDGE,"E3.sketch_text.stroke-135"),sQuery(id+"F2.wireOp",EDGE,"E3.sketch_text.stroke-136"),sQuery(id+"F2.wireOp",EDGE,"E3.sketch_text.stroke-137"),sQuery(id+"F2.wireOp",EDGE,"E3.sketch_text.stroke-138"),sQuery(id+"F2.wireOp",EDGE,"E3.sketch_text.stroke-139"),sQuery(id+"F2.wireOp",EDGE,"E3.sketch_text.stroke-140"),sQuery(id+"F2.wireOp",EDGE,"E3.sketch_text.stroke-141"),sQuery(id+"F2.wireOp",EDGE,"E3.sketch_text.stroke-142"),sQuery(id+"F2.wireOp",EDGE,"E3.sketch_text.stroke-143"),sQuery(id+"F2.wireOp",EDGE,"E3.sketch_text.stroke-144"),sQuery(id+"F2.wireOp",EDGE,"E3.sketch_text.stroke-145"),sQuery(id+"F2.wireOp",EDGE,"E3.sketch_text.stroke-146"),sQuery(id+"F2.wireOp",EDGE,"E3.sketch_text.stroke-147"),sQuery(id+"F2.wireOp",EDGE,"E3.sketch_text.stroke-148"),sQuery(id+"F2.wireOp",EDGE,"E3.sketch_text.stroke-149"),sQuery(id+"F2.wireOp",EDGE,"E3.sketch_text.stroke-150"),sQuery(id+"F2.wireOp",EDGE,"E3.sketch_text.stroke-151"),sQuery(id+"F2.wireOp",EDGE,"E3.sketch_text.stroke-152"),sQuery(id+"F2.wireOp",EDGE,"E3.sketch_text.stroke-153"),sQuery(id+"F2.wireOp",EDGE,"E3.sketch_text.stroke-154"),sQuery(id+"F2.wireOp",EDGE,"E3.sketch_text.stroke-155"),sQuery(id+"F2.wireOp",EDGE,"E3.sketch_text.stroke-156"),sQuery(id+"F2.wireOp",EDGE,"E3.sketch_text.stroke-157")])]});
            var Q11;
            Q11=makeQuery(id+"F3.opExtrude","SWEPT_BODY",BODY,{"disambiguationData":[OSD([sQuery(id+"F2.wireOp",EDGE,"E3.sketch_text.stroke-158"),sQuery(id+"F2.wireOp",EDGE,"E3.sketch_text.stroke-159"),sQuery(id+"F2.wireOp",EDGE,"E3.sketch_text.stroke-160"),sQuery(id+"F2.wireOp",EDGE,"E3.sketch_text.stroke-161"),sQuery(id+"F2.wireOp",EDGE,"E3.sketch_text.stroke-162"),sQuery(id+"F2.wireOp",EDGE,"E3.sketch_text.stroke-163"),sQuery(id+"F2.wireOp",EDGE,"E3.sketch_text.stroke-164"),sQuery(id+"F2.wireOp",EDGE,"E3.sketch_text.stroke-165"),sQuery(id+"F2.wireOp",EDGE,"E3.sketch_text.stroke-166"),sQuery(id+"F2.wireOp",EDGE,"E3.sketch_text.stroke-167"),sQuery(id+"F2.wireOp",EDGE,"E3.sketch_text.stroke-168"),sQuery(id+"F2.wireOp",EDGE,"E3.sketch_text.stroke-169"),sQuery(id+"F2.wireOp",EDGE,"E3.sketch_text.stroke-170"),sQuery(id+"F2.wireOp",EDGE,"E3.sketch_text.stroke-171"),sQuery(id+"F2.wireOp",EDGE,"E3.sketch_text.stroke-172"),sQuery(id+"F2.wireOp",EDGE,"E3.sketch_text.stroke-173"),sQuery(id+"F2.wireOp",EDGE,"E3.sketch_text.stroke-174"),sQuery(id+"F2.wireOp",EDGE,"E3.sketch_text.stroke-175"),sQuery(id+"F2.wireOp",EDGE,"E3.sketch_text.stroke-176"),sQuery(id+"F2.wireOp",EDGE,"E3.sketch_text.stroke-177")])]});
            var Q12;
            Q12=makeQuery(id+"F3.opExtrude","SWEPT_BODY",BODY,{"disambiguationData":[OSD([sQuery(id+"F2.wireOp",EDGE,"E3.sketch_text.stroke-178"),sQuery(id+"F2.wireOp",EDGE,"E3.sketch_text.stroke-179"),sQuery(id+"F2.wireOp",EDGE,"E3.sketch_text.stroke-180"),sQuery(id+"F2.wireOp",EDGE,"E3.sketch_text.stroke-181"),sQuery(id+"F2.wireOp",EDGE,"E3.sketch_text.stroke-182"),sQuery(id+"F2.wireOp",EDGE,"E3.sketch_text.stroke-183"),sQuery(id+"F2.wireOp",EDGE,"E3.sketch_text.stroke-184"),sQuery(id+"F2.wireOp",EDGE,"E3.sketch_text.stroke-185"),sQuery(id+"F2.wireOp",EDGE,"E3.sketch_text.stroke-186"),sQuery(id+"F2.wireOp",EDGE,"E3.sketch_text.stroke-187"),sQuery(id+"F2.wireOp",EDGE,"E3.sketch_text.stroke-188"),sQuery(id+"F2.wireOp",EDGE,"E3.sketch_text.stroke-189"),sQuery(id+"F2.wireOp",EDGE,"E3.sketch_text.stroke-190"),sQuery(id+"F2.wireOp",EDGE,"E3.sketch_text.stroke-191"),sQuery(id+"F2.wireOp",EDGE,"E3.sketch_text.stroke-192"),sQuery(id+"F2.wireOp",EDGE,"E3.sketch_text.stroke-193"),sQuery(id+"F2.wireOp",EDGE,"E3.sketch_text.stroke-194"),sQuery(id+"F2.wireOp",EDGE,"E3.sketch_text.stroke-195")])]});
            transform(context, id + "F9", {"entities" : qUnion([Q0, Q1, Q2, Q3, Q4, Q5, Q6, Q7, Q8, Q9, Q10, Q11, Q12]), "transformType" : TransformType.TRANSLATION_3D, "dx" : 0 * mm, "dy" : 0 * mm, "dz" : -1.3 * mm, "makeCopy" : false});
        }
        {
            var Q0;
            Q0=makeQuery(id+"F3.opExtrude","SWEPT_BODY",BODY,{"disambiguationData":[OSD([sQuery(id+"F2.wireOp",EDGE,"E3.sketch_text.stroke-0"),sQuery(id+"F2.wireOp",EDGE,"E3.sketch_text.stroke-1"),sQuery(id+"F2.wireOp",EDGE,"E3.sketch_text.stroke-2"),sQuery(id+"F2.wireOp",EDGE,"E3.sketch_text.stroke-3"),sQuery(id+"F2.wireOp",EDGE,"E3.sketch_text.stroke-4"),sQuery(id+"F2.wireOp",EDGE,"E3.sketch_text.stroke-5"),sQuery(id+"F2.wireOp",EDGE,"E3.sketch_text.stroke-6"),sQuery(id+"F2.wireOp",EDGE,"E3.sketch_text.stroke-7"),sQuery(id+"F2.wireOp",EDGE,"E3.sketch_text.stroke-8"),sQuery(id+"F2.wireOp",EDGE,"E3.sketch_text.stroke-9"),sQuery(id+"F2.wireOp",EDGE,"E3.sketch_text.stroke-10"),sQuery(id+"F2.wireOp",EDGE,"E3.sketch_text.stroke-11")])]});
            var Q1;
            Q1=makeQuery(id+"F3.opExtrude","SWEPT_BODY",BODY,{"disambiguationData":[OSD([sQuery(id+"F2.wireOp",EDGE,"E3.sketch_text.stroke-12"),sQuery(id+"F2.wireOp",EDGE,"E3.sketch_text.stroke-13"),sQuery(id+"F2.wireOp",EDGE,"E3.sketch_text.stroke-14"),sQuery(id+"F2.wireOp",EDGE,"E3.sketch_text.stroke-15"),sQuery(id+"F2.wireOp",EDGE,"E3.sketch_text.stroke-16"),sQuery(id+"F2.wireOp",EDGE,"E3.sketch_text.stroke-17"),sQuery(id+"F2.wireOp",EDGE,"E3.sketch_text.stroke-18"),sQuery(id+"F2.wireOp",EDGE,"E3.sketch_text.stroke-19"),sQuery(id+"F2.wireOp",EDGE,"E3.sketch_text.stroke-20"),sQuery(id+"F2.wireOp",EDGE,"E3.sketch_text.stroke-21"),sQuery(id+"F2.wireOp",EDGE,"E3.sketch_text.stroke-22"),sQuery(id+"F2.wireOp",EDGE,"E3.sketch_text.stroke-23"),sQuery(id+"F2.wireOp",EDGE,"E3.sketch_text.stroke-24"),sQuery(id+"F2.wireOp",EDGE,"E3.sketch_text.stroke-25"),sQuery(id+"F2.wireOp",EDGE,"E3.sketch_text.stroke-26"),sQuery(id+"F2.wireOp",EDGE,"E3.sketch_text.stroke-27"),sQuery(id+"F2.wireOp",EDGE,"E3.sketch_text.stroke-28"),sQuery(id+"F2.wireOp",EDGE,"E3.sketch_text.stroke-29"),sQuery(id+"F2.wireOp",EDGE,"E3.sketch_text.stroke-30")])]});
            var Q2;
            Q2=makeQuery(id+"F3.opExtrude","SWEPT_BODY",BODY,{"disambiguationData":[OSD([sQuery(id+"F2.wireOp",EDGE,"E3.sketch_text.stroke-31"),sQuery(id+"F2.wireOp",EDGE,"E3.sketch_text.stroke-32"),sQuery(id+"F2.wireOp",EDGE,"E3.sketch_text.stroke-33"),sQuery(id+"F2.wireOp",EDGE,"E3.sketch_text.stroke-34"),sQuery(id+"F2.wireOp",EDGE,"E3.sketch_text.stroke-35"),sQuery(id+"F2.wireOp",EDGE,"E3.sketch_text.stroke-36"),sQuery(id+"F2.wireOp",EDGE,"E3.sketch_text.stroke-37"),sQuery(id+"F2.wireOp",EDGE,"E3.sketch_text.stroke-38"),sQuery(id+"F2.wireOp",EDGE,"E3.sketch_text.stroke-39"),sQuery(id+"F2.wireOp",EDGE,"E3.sketch_text.stroke-40")])]});
            var Q3;
            Q3=makeQuery(id+"F3.opExtrude","SWEPT_BODY",BODY,{"disambiguationData":[OSD([sQuery(id+"F2.wireOp",EDGE,"E3.sketch_text.stroke-41"),sQuery(id+"F2.wireOp",EDGE,"E3.sketch_text.stroke-42"),sQuery(id+"F2.wireOp",EDGE,"E3.sketch_text.stroke-43"),sQuery(id+"F2.wireOp",EDGE,"E3.sketch_text.stroke-44"),sQuery(id+"F2.wireOp",EDGE,"E3.sketch_text.stroke-45"),sQuery(id+"F2.wireOp",EDGE,"E3.sketch_text.stroke-46"),sQuery(id+"F2.wireOp",EDGE,"E3.sketch_text.stroke-47"),sQuery(id+"F2.wireOp",EDGE,"E3.sketch_text.stroke-48"),sQuery(id+"F2.wireOp",EDGE,"E3.sketch_text.stroke-49"),sQuery(id+"F2.wireOp",EDGE,"E3.sketch_text.stroke-50")])]});
            var Q4;
            Q4=makeQuery(id+"F3.opExtrude","SWEPT_BODY",BODY,{"disambiguationData":[OSD([sQuery(id+"F2.wireOp",EDGE,"E3.sketch_text.stroke-51"),sQuery(id+"F2.wireOp",EDGE,"E3.sketch_text.stroke-52"),sQuery(id+"F2.wireOp",EDGE,"E3.sketch_text.stroke-53"),sQuery(id+"F2.wireOp",EDGE,"E3.sketch_text.stroke-54"),sQuery(id+"F2.wireOp",EDGE,"E3.sketch_text.stroke-55"),sQuery(id+"F2.wireOp",EDGE,"E3.sketch_text.stroke-56"),sQuery(id+"F2.wireOp",EDGE,"E3.sketch_text.stroke-57"),sQuery(id+"F2.wireOp",EDGE,"E3.sketch_text.stroke-58"),sQuery(id+"F2.wireOp",EDGE,"E3.sketch_text.stroke-59"),sQuery(id+"F2.wireOp",EDGE,"E3.sketch_text.stroke-60"),sQuery(id+"F2.wireOp",EDGE,"E3.sketch_text.stroke-61"),sQuery(id+"F2.wireOp",EDGE,"E3.sketch_text.stroke-62"),sQuery(id+"F2.wireOp",EDGE,"E3.sketch_text.stroke-63"),sQuery(id+"F2.wireOp",EDGE,"E3.sketch_text.stroke-64"),sQuery(id+"F2.wireOp",EDGE,"E3.sketch_text.stroke-65")])]});
            var Q5;
            Q5=makeQuery(id+"F3.opExtrude","SWEPT_BODY",BODY,{"disambiguationData":[OSD([sQuery(id+"F2.wireOp",EDGE,"E3.sketch_text.stroke-66"),sQuery(id+"F2.wireOp",EDGE,"E3.sketch_text.stroke-67"),sQuery(id+"F2.wireOp",EDGE,"E3.sketch_text.stroke-68"),sQuery(id+"F2.wireOp",EDGE,"E3.sketch_text.stroke-69"),sQuery(id+"F2.wireOp",EDGE,"E3.sketch_text.stroke-70"),sQuery(id+"F2.wireOp",EDGE,"E3.sketch_text.stroke-71"),sQuery(id+"F2.wireOp",EDGE,"E3.sketch_text.stroke-72"),sQuery(id+"F2.wireOp",EDGE,"E3.sketch_text.stroke-73"),sQuery(id+"F2.wireOp",EDGE,"E3.sketch_text.stroke-74"),sQuery(id+"F2.wireOp",EDGE,"E3.sketch_text.stroke-75"),sQuery(id+"F2.wireOp",EDGE,"E3.sketch_text.stroke-76"),sQuery(id+"F2.wireOp",EDGE,"E3.sketch_text.stroke-77"),sQuery(id+"F2.wireOp",EDGE,"E3.sketch_text.stroke-78"),sQuery(id+"F2.wireOp",EDGE,"E3.sketch_text.stroke-79"),sQuery(id+"F2.wireOp",EDGE,"E3.sketch_text.stroke-80"),sQuery(id+"F2.wireOp",EDGE,"E3.sketch_text.stroke-81"),sQuery(id+"F2.wireOp",EDGE,"E3.sketch_text.stroke-82"),sQuery(id+"F2.wireOp",EDGE,"E3.sketch_text.stroke-83")])]});
            var Q6;
            Q6=makeQuery(id+"F3.opExtrude","SWEPT_BODY",BODY,{"disambiguationData":[OSD([sQuery(id+"F2.wireOp",EDGE,"E3.sketch_text.stroke-84"),sQuery(id+"F2.wireOp",EDGE,"E3.sketch_text.stroke-85"),sQuery(id+"F2.wireOp",EDGE,"E3.sketch_text.stroke-86"),sQuery(id+"F2.wireOp",EDGE,"E3.sketch_text.stroke-87")])]});
            var Q7;
            Q7=makeQuery(id+"F3.opExtrude","SWEPT_BODY",BODY,{"disambiguationData":[OSD([sQuery(id+"F2.wireOp",EDGE,"E3.sketch_text.stroke-92"),sQuery(id+"F2.wireOp",EDGE,"E3.sketch_text.stroke-93"),sQuery(id+"F2.wireOp",EDGE,"E3.sketch_text.stroke-94"),sQuery(id+"F2.wireOp",EDGE,"E3.sketch_text.stroke-95"),sQuery(id+"F2.wireOp",EDGE,"E3.sketch_text.stroke-96"),sQuery(id+"F2.wireOp",EDGE,"E3.sketch_text.stroke-97"),sQuery(id+"F2.wireOp",EDGE,"E3.sketch_text.stroke-98"),sQuery(id+"F2.wireOp",EDGE,"E3.sketch_text.stroke-99"),sQuery(id+"F2.wireOp",EDGE,"E3.sketch_text.stroke-100"),sQuery(id+"F2.wireOp",EDGE,"E3.sketch_text.stroke-101"),sQuery(id+"F2.wireOp",EDGE,"E3.sketch_text.stroke-102"),sQuery(id+"F2.wireOp",EDGE,"E3.sketch_text.stroke-103"),sQuery(id+"F2.wireOp",EDGE,"E3.sketch_text.stroke-104"),sQuery(id+"F2.wireOp",EDGE,"E3.sketch_text.stroke-105"),sQuery(id+"F2.wireOp",EDGE,"E3.sketch_text.stroke-106"),sQuery(id+"F2.wireOp",EDGE,"E3.sketch_text.stroke-107"),sQuery(id+"F2.wireOp",EDGE,"E3.sketch_text.stroke-108"),sQuery(id+"F2.wireOp",EDGE,"E3.sketch_text.stroke-109"),sQuery(id+"F2.wireOp",EDGE,"E3.sketch_text.stroke-110"),sQuery(id+"F2.wireOp",EDGE,"E3.sketch_text.stroke-111")])]});
            var Q8;
            Q8=makeQuery(id+"F3.opExtrude","SWEPT_BODY",BODY,{"disambiguationData":[OSD([sQuery(id+"F2.wireOp",EDGE,"E3.sketch_text.stroke-88"),sQuery(id+"F2.wireOp",EDGE,"E3.sketch_text.stroke-89"),sQuery(id+"F2.wireOp",EDGE,"E3.sketch_text.stroke-90"),sQuery(id+"F2.wireOp",EDGE,"E3.sketch_text.stroke-91")])]});
            var Q9;
            Q9=makeQuery(id+"F3.opExtrude","SWEPT_BODY",BODY,{"disambiguationData":[OSD([sQuery(id+"F2.wireOp",EDGE,"E3.sketch_text.stroke-112"),sQuery(id+"F2.wireOp",EDGE,"E3.sketch_text.stroke-113"),sQuery(id+"F2.wireOp",EDGE,"E3.sketch_text.stroke-114"),sQuery(id+"F2.wireOp",EDGE,"E3.sketch_text.stroke-115"),sQuery(id+"F2.wireOp",EDGE,"E3.sketch_text.stroke-116"),sQuery(id+"F2.wireOp",EDGE,"E3.sketch_text.stroke-117"),sQuery(id+"F2.wireOp",EDGE,"E3.sketch_text.stroke-118"),sQuery(id+"F2.wireOp",EDGE,"E3.sketch_text.stroke-119"),sQuery(id+"F2.wireOp",EDGE,"E3.sketch_text.stroke-120"),sQuery(id+"F2.wireOp",EDGE,"E3.sketch_text.stroke-121"),sQuery(id+"F2.wireOp",EDGE,"E3.sketch_text.stroke-122"),sQuery(id+"F2.wireOp",EDGE,"E3.sketch_text.stroke-123"),sQuery(id+"F2.wireOp",EDGE,"E3.sketch_text.stroke-124"),sQuery(id+"F2.wireOp",EDGE,"E3.sketch_text.stroke-125"),sQuery(id+"F2.wireOp",EDGE,"E3.sketch_text.stroke-126"),sQuery(id+"F2.wireOp",EDGE,"E3.sketch_text.stroke-127"),sQuery(id+"F2.wireOp",EDGE,"E3.sketch_text.stroke-128"),sQuery(id+"F2.wireOp",EDGE,"E3.sketch_text.stroke-129")])]});
            var Q10;
            Q10=makeQuery(id+"F3.opExtrude","SWEPT_BODY",BODY,{"disambiguationData":[OSD([sQuery(id+"F2.wireOp",EDGE,"E3.sketch_text.stroke-130"),sQuery(id+"F2.wireOp",EDGE,"E3.sketch_text.stroke-131"),sQuery(id+"F2.wireOp",EDGE,"E3.sketch_text.stroke-132"),sQuery(id+"F2.wireOp",EDGE,"E3.sketch_text.stroke-133"),sQuery(id+"F2.wireOp",EDGE,"E3.sketch_text.stroke-134"),sQuery(id+"F2.wireOp",EDGE,"E3.sketch_text.stroke-135"),sQuery(id+"F2.wireOp",EDGE,"E3.sketch_text.stroke-136"),sQuery(id+"F2.wireOp",EDGE,"E3.sketch_text.stroke-137"),sQuery(id+"F2.wireOp",EDGE,"E3.sketch_text.stroke-138"),sQuery(id+"F2.wireOp",EDGE,"E3.sketch_text.stroke-139"),sQuery(id+"F2.wireOp",EDGE,"E3.sketch_text.stroke-140"),sQuery(id+"F2.wireOp",EDGE,"E3.sketch_text.stroke-141"),sQuery(id+"F2.wireOp",EDGE,"E3.sketch_text.stroke-142"),sQuery(id+"F2.wireOp",EDGE,"E3.sketch_text.stroke-143"),sQuery(id+"F2.wireOp",EDGE,"E3.sketch_text.stroke-144"),sQuery(id+"F2.wireOp",EDGE,"E3.sketch_text.stroke-145"),sQuery(id+"F2.wireOp",EDGE,"E3.sketch_text.stroke-146"),sQuery(id+"F2.wireOp",EDGE,"E3.sketch_text.stroke-147"),sQuery(id+"F2.wireOp",EDGE,"E3.sketch_text.stroke-148"),sQuery(id+"F2.wireOp",EDGE,"E3.sketch_text.stroke-149"),sQuery(id+"F2.wireOp",EDGE,"E3.sketch_text.stroke-150"),sQuery(id+"F2.wireOp",EDGE,"E3.sketch_text.stroke-151"),sQuery(id+"F2.wireOp",EDGE,"E3.sketch_text.stroke-152"),sQuery(id+"F2.wireOp",EDGE,"E3.sketch_text.stroke-153"),sQuery(id+"F2.wireOp",EDGE,"E3.sketch_text.stroke-154"),sQuery(id+"F2.wireOp",EDGE,"E3.sketch_text.stroke-155"),sQuery(id+"F2.wireOp",EDGE,"E3.sketch_text.stroke-156"),sQuery(id+"F2.wireOp",EDGE,"E3.sketch_text.stroke-157")])]});
            var Q11;
            Q11=makeQuery(id+"F3.opExtrude","SWEPT_BODY",BODY,{"disambiguationData":[OSD([sQuery(id+"F2.wireOp",EDGE,"E3.sketch_text.stroke-158"),sQuery(id+"F2.wireOp",EDGE,"E3.sketch_text.stroke-159"),sQuery(id+"F2.wireOp",EDGE,"E3.sketch_text.stroke-160"),sQuery(id+"F2.wireOp",EDGE,"E3.sketch_text.stroke-161"),sQuery(id+"F2.wireOp",EDGE,"E3.sketch_text.stroke-162"),sQuery(id+"F2.wireOp",EDGE,"E3.sketch_text.stroke-163"),sQuery(id+"F2.wireOp",EDGE,"E3.sketch_text.stroke-164"),sQuery(id+"F2.wireOp",EDGE,"E3.sketch_text.stroke-165"),sQuery(id+"F2.wireOp",EDGE,"E3.sketch_text.stroke-166"),sQuery(id+"F2.wireOp",EDGE,"E3.sketch_text.stroke-167"),sQuery(id+"F2.wireOp",EDGE,"E3.sketch_text.stroke-168"),sQuery(id+"F2.wireOp",EDGE,"E3.sketch_text.stroke-169"),sQuery(id+"F2.wireOp",EDGE,"E3.sketch_text.stroke-170"),sQuery(id+"F2.wireOp",EDGE,"E3.sketch_text.stroke-171"),sQuery(id+"F2.wireOp",EDGE,"E3.sketch_text.stroke-172"),sQuery(id+"F2.wireOp",EDGE,"E3.sketch_text.stroke-173"),sQuery(id+"F2.wireOp",EDGE,"E3.sketch_text.stroke-174"),sQuery(id+"F2.wireOp",EDGE,"E3.sketch_text.stroke-175"),sQuery(id+"F2.wireOp",EDGE,"E3.sketch_text.stroke-176"),sQuery(id+"F2.wireOp",EDGE,"E3.sketch_text.stroke-177")])]});
            var Q12;
            Q12=makeQuery(id+"F3.opExtrude","SWEPT_BODY",BODY,{"disambiguationData":[OSD([sQuery(id+"F2.wireOp",EDGE,"E3.sketch_text.stroke-178"),sQuery(id+"F2.wireOp",EDGE,"E3.sketch_text.stroke-179"),sQuery(id+"F2.wireOp",EDGE,"E3.sketch_text.stroke-180"),sQuery(id+"F2.wireOp",EDGE,"E3.sketch_text.stroke-181"),sQuery(id+"F2.wireOp",EDGE,"E3.sketch_text.stroke-182"),sQuery(id+"F2.wireOp",EDGE,"E3.sketch_text.stroke-183"),sQuery(id+"F2.wireOp",EDGE,"E3.sketch_text.stroke-184"),sQuery(id+"F2.wireOp",EDGE,"E3.sketch_text.stroke-185"),sQuery(id+"F2.wireOp",EDGE,"E3.sketch_text.stroke-186"),sQuery(id+"F2.wireOp",EDGE,"E3.sketch_text.stroke-187"),sQuery(id+"F2.wireOp",EDGE,"E3.sketch_text.stroke-188"),sQuery(id+"F2.wireOp",EDGE,"E3.sketch_text.stroke-189"),sQuery(id+"F2.wireOp",EDGE,"E3.sketch_text.stroke-190"),sQuery(id+"F2.wireOp",EDGE,"E3.sketch_text.stroke-191"),sQuery(id+"F2.wireOp",EDGE,"E3.sketch_text.stroke-192"),sQuery(id+"F2.wireOp",EDGE,"E3.sketch_text.stroke-193"),sQuery(id+"F2.wireOp",EDGE,"E3.sketch_text.stroke-194"),sQuery(id+"F2.wireOp",EDGE,"E3.sketch_text.stroke-195")])]});
            var Q13;
            Q13=makeQuery(id+"F1.opExtrude","SWEPT_BODY",BODY,{"disambiguationData":[OSD([sQuery(id+"F0.wireOp",EDGE,"E0.bottom"),sQuery(id+"F0.wireOp",EDGE,"E0.top"),sQuery(id+"F0.wireOp",EDGE,"E0.left"),sQuery(id+"F0.wireOp",EDGE,"E0.right"),sQuery(id+"F0.wireOp",EDGE,"E1.bottom"),sQuery(id+"F0.wireOp",EDGE,"E1.top"),sQuery(id+"F0.wireOp",EDGE,"E1.left"),sQuery(id+"F0.wireOp",EDGE,"E1.right")])]});
            booleanBodies(context, id + "F10", {"operationType" : BooleanOperationType.SUBTRACTION, "tools" : qUnion([Q0, Q1, Q2, Q3, Q4, Q5, Q6, Q7, Q8, Q9, Q10, Q11, Q12]), "targets" : qUnion([Q13])});
        }
    });
